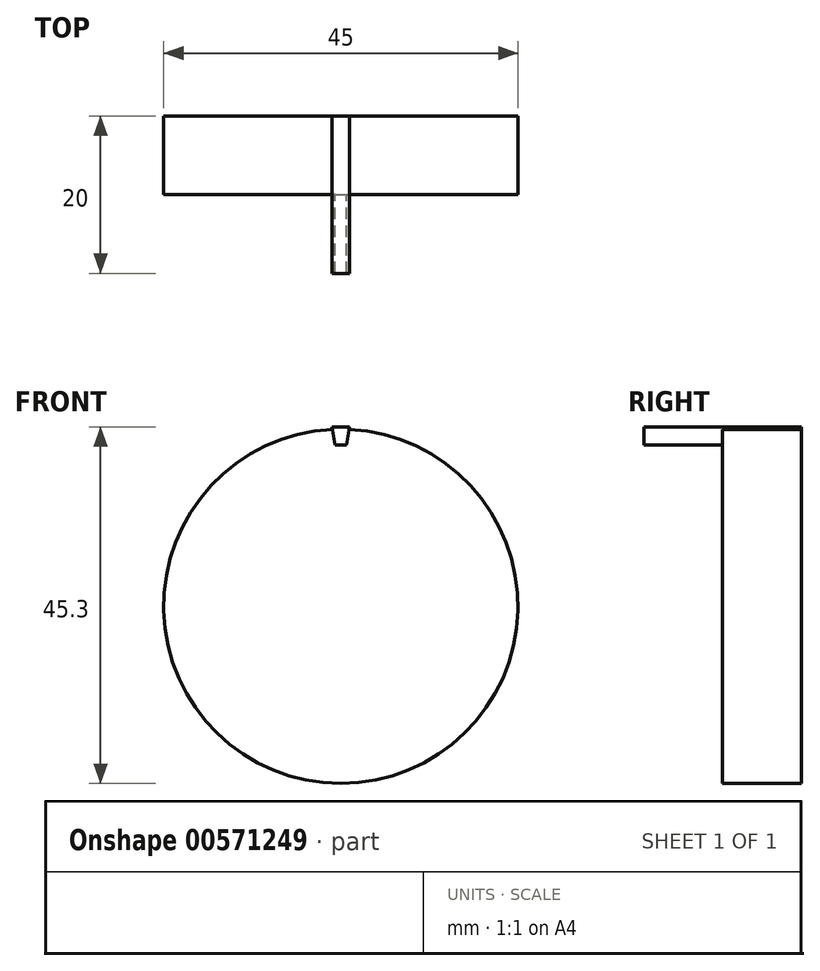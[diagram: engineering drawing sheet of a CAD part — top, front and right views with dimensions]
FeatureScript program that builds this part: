
annotation { "Feature Type Name" : "Feature", "Feature Type Description" : "" }
export const myFeature = defineFeature(function(context is Context, id is Id, definition is map)
    precondition{}
    {
        {
            var Q0;
            Q0=qCreatedBy(makeId("Front.planeOp"),FACE);
            var sketch = newSketch(context, id + "F0", { "sketchPlane" : qUnion([Q0])});
            skCircle(sketch, "E0", {"center": v(0, 0) * mm, "radius": 22.5 * mm});
            skLineSegment(sketch, "E1", {"start": v(-0.75, 20.5) * mm, "end": v(-1.13, 22.8) * mm});
            skLineSegment(sketch, "E2.MirrorCS", {"start": v(0.75, 20.5) * mm, "end": v(1.13, 22.8) * mm});
            skLineSegment(sketch, "E3", {"start": v(-1.13, 22.8) * mm, "end": v(1.13, 22.8) * mm});
            skLineSegment(sketch, "E4", {"start": v(-0.75, 20.5) * mm, "end": v(0.75, 20.5) * mm});
            skSolve(sketch);
        }
        {
            var Q0;
            {var subQ5=sQuery(id+"F0.wireOp",EDGE,"E4");Q0=makeQuery(id+"F0.imprint","IMPRINT",FACE,{"disambiguationData":[TD([[makeQuery(id+"F0.imprint","IMPRINT",EDGE,{"derivedFrom":subQ5}),1.0]])]});}
            var Q1;
            {var subQ5=sQuery(id+"F0.wireOp",EDGE,"E3");Q1=makeQuery(id+"F0.imprint","IMPRINT",FACE,{"disambiguationData":[TD([[makeQuery(id+"F0.imprint","IMPRINT",EDGE,{"derivedFrom":subQ5}),-1.0]])]});}
            extrude(context, id + "F1", {"entities" : qUnion([Q0, Q1]), "depth" : 20 * mm, "offsetDistance" : 25 * mm});
        }
        {
            var Q0;
            {var subQ5=sQuery(id+"F0.wireOp",EDGE,"E4");Q0=makeQuery(id+"F0.imprint","IMPRINT",FACE,{"disambiguationData":[TD([[makeQuery(id+"F0.imprint","IMPRINT",EDGE,{"derivedFrom":subQ5}),-1.0]])]});}
            extrude(context, id + "F2", {"entities" : qUnion([Q0]), "operationType" : NewBodyOperationType.ADD, "depth" : 10 * mm, "offsetDistance" : 25 * mm});
        }
    });
